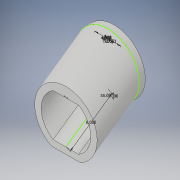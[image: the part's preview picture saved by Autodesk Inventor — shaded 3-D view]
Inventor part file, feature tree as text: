
AUTODESK INVENTOR PART (.ipt)
format: ipt  version: 2017 (Build 210142000, 142)  size: 174,080 bytes
history: native  units: in
note: dims shown in document units (in); Inventor stores cm internally (conversion verified against a paired STEP export)
features: sketch x2, extrude x2, sweep x2, plane x1
ambient origin geometry x8: Origin, YZ Plane, XZ Plane, XY Plane, X Axis, Y Axis, Z Axis, Center Point
bodies: Solid1 (feature_tree), Solid2 (feature_tree), Solid3 (feature_tree)
feature tree (7):
  sketch  "Sketch1"  dims[d0=6.6667in d1=4.0in d2=1.0in d3=1.0in d4=0.0in d12=8.0in]
  extrude  "connecction top"  Depth=1.0in
  extrude  "light flat"  Depth=1.0in
  plane  "Work Plane2"
  sketch  "Sketch6"  dims[d28=8.0in d29=0.3779in d34=0.5833in d35=0.0625in d36=0.0625in d37=0.125in d38=0.25in d39=0.125in d40=45.0deg d41=0.0892in d42=0.0884in d43=1.0in d44=0.0in d45=0.0in d46=0.0in d47=0.0in d48=0.0in]
  sweep  "ramp"
  sweep  "light angle"
